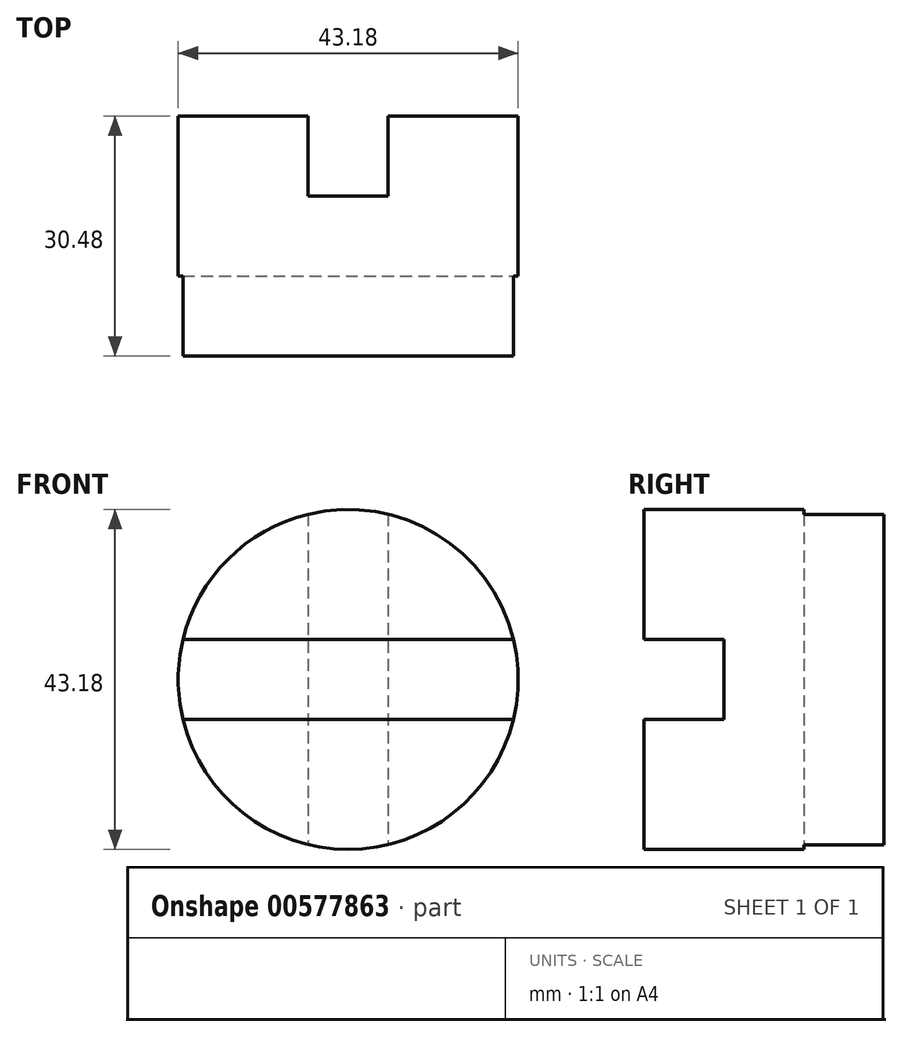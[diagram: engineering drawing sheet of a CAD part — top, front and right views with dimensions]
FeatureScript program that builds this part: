
annotation { "Feature Type Name" : "Feature", "Feature Type Description" : "" }
export const myFeature = defineFeature(function(context is Context, id is Id, definition is map)
    precondition{}
    {
        {
            var Q0;
            Q0=qCreatedBy(makeId("Front.planeOp"),FACE);
            var sketch = newSketch(context, id + "F0", { "sketchPlane" : qUnion([Q0])});
            skCircle(sketch, "E0", {"center": v(0, 0) * mm, "radius": 21.59 * mm});
            skSolve(sketch);
        }
        {
            var Q0;
            Q0=makeQuery(id+"F0.imprint","IMPRINT",FACE,{"disambiguationData":[TD([[makeQuery(id+"F0.imprint","IMPRINT",EDGE,{"derivedFrom":sQuery(id+"F0.wireOp",EDGE,"E0")}),1.0]])]});
            extrude(context, id + "F1", {"entities" : qUnion([Q0]), "endBound" : BoundingType.SYMMETRIC, "depth" : 30.48 * mm, "offsetDistance" : 25.4 * mm});
        }
        {
            var Q0;
            Q0=makeQuery(id+"F1.opExtrude","CAP_FACE",FACE,{"disambiguationData":[OSD([sQuery(id+"F0.wireOp",EDGE,"E0")])],"isStart":false});
            var sketch = newSketch(context, id + "F2", { "sketchPlane" : qUnion([Q0])});
            skLineSegment(sketch, "E1.bottom", {"start": v(-20.98, -5.08) * mm, "end": v(20.98, -5.08) * mm});
            skLineSegment(sketch, "E1.top", {"start": v(-20.98, 5.08) * mm, "end": v(20.98, 5.08) * mm});
            skLineSegment(sketch, "E1.left", {"start": v(-20.98, -5.08) * mm, "end": v(-20.98, 5.08) * mm});
            skLineSegment(sketch, "E1.right", {"start": v(20.98, -5.08) * mm, "end": v(20.98, 5.08) * mm});
            skPoint(sketch, "E1.middle", {"position": v(0, 0) * mm});
            skSolve(sketch);
        }
        {
            var Q0;
            Q0=makeQuery(id+"F2.imprint","IMPRINT",FACE,{"disambiguationData":[TD([[makeQuery(id+"F2.imprint","IMPRINT",EDGE,{"derivedFrom":sQuery(id+"F2.wireOp",EDGE,"E1.bottom")}),1.0]])]});
            var Q1;
            {var subQ0=sQuery(id+"F2.wireOp",EDGE,"E1.left");Q1=makeQuery(id+"F2.imprint","IMPRINT",FACE,{"disambiguationData":[TD([[makeQuery(id+"F2.imprint","IMPRINT",EDGE,{"derivedFrom":subQ0}),1.0]])]});}
            var Q2;
            {var subQ0=sQuery(id+"F2.wireOp",EDGE,"E1.right");Q2=makeQuery(id+"F2.imprint","IMPRINT",FACE,{"disambiguationData":[TD([[makeQuery(id+"F2.imprint","IMPRINT",EDGE,{"derivedFrom":subQ0}),-1.0]])]});}
            extrude(context, id + "F3", {"entities" : qUnion([Q0, Q1, Q2]), "operationType" : NewBodyOperationType.REMOVE, "oppositeDirection" : true, "depth" : 10.16 * mm, "offsetDistance" : 25.4 * mm});
        }
        {
            var Q0;
            Q0=makeQuery(id+"F1.opExtrude","CAP_FACE",FACE,{"disambiguationData":[OSD([sQuery(id+"F0.wireOp",EDGE,"E0")])],"isStart":true});
            var sketch = newSketch(context, id + "F4", { "sketchPlane" : qUnion([Q0])});
            skLineSegment(sketch, "E2.bottom", {"start": v(-5.08, 20.98) * mm, "end": v(5.08, 20.98) * mm});
            skLineSegment(sketch, "E2.top", {"start": v(-5.08, -20.98) * mm, "end": v(5.08, -20.98) * mm});
            skLineSegment(sketch, "E2.left", {"start": v(-5.08, 20.98) * mm, "end": v(-5.08, -20.98) * mm});
            skLineSegment(sketch, "E2.right", {"start": v(5.08, 20.98) * mm, "end": v(5.08, -20.98) * mm});
            skPoint(sketch, "E2.middle", {"position": v(0, 0) * mm});
            skSolve(sketch);
        }
        {
            var Q0;
            {var subQ0=sQuery(id+"F4.wireOp",EDGE,"E2.bottom");Q0=makeQuery(id+"F4.imprint","IMPRINT",FACE,{"disambiguationData":[TD([[makeQuery(id+"F4.imprint","IMPRINT",EDGE,{"derivedFrom":subQ0}),1.0]])]});}
            var Q1;
            Q1=makeQuery(id+"F4.imprint","IMPRINT",FACE,{"disambiguationData":[TD([[makeQuery(id+"F4.imprint","IMPRINT",EDGE,{"derivedFrom":sQuery(id+"F4.wireOp",EDGE,"E2.bottom")}),-1.0]])]});
            var Q2;
            {var subQ0=sQuery(id+"F4.wireOp",EDGE,"E2.top");Q2=makeQuery(id+"F4.imprint","IMPRINT",FACE,{"disambiguationData":[TD([[makeQuery(id+"F4.imprint","IMPRINT",EDGE,{"derivedFrom":subQ0}),-1.0]])]});}
            extrude(context, id + "F5", {"entities" : qUnion([Q0, Q1, Q2]), "operationType" : NewBodyOperationType.REMOVE, "oppositeDirection" : true, "depth" : 10.16 * mm, "offsetDistance" : 25.4 * mm});
        }
    });
